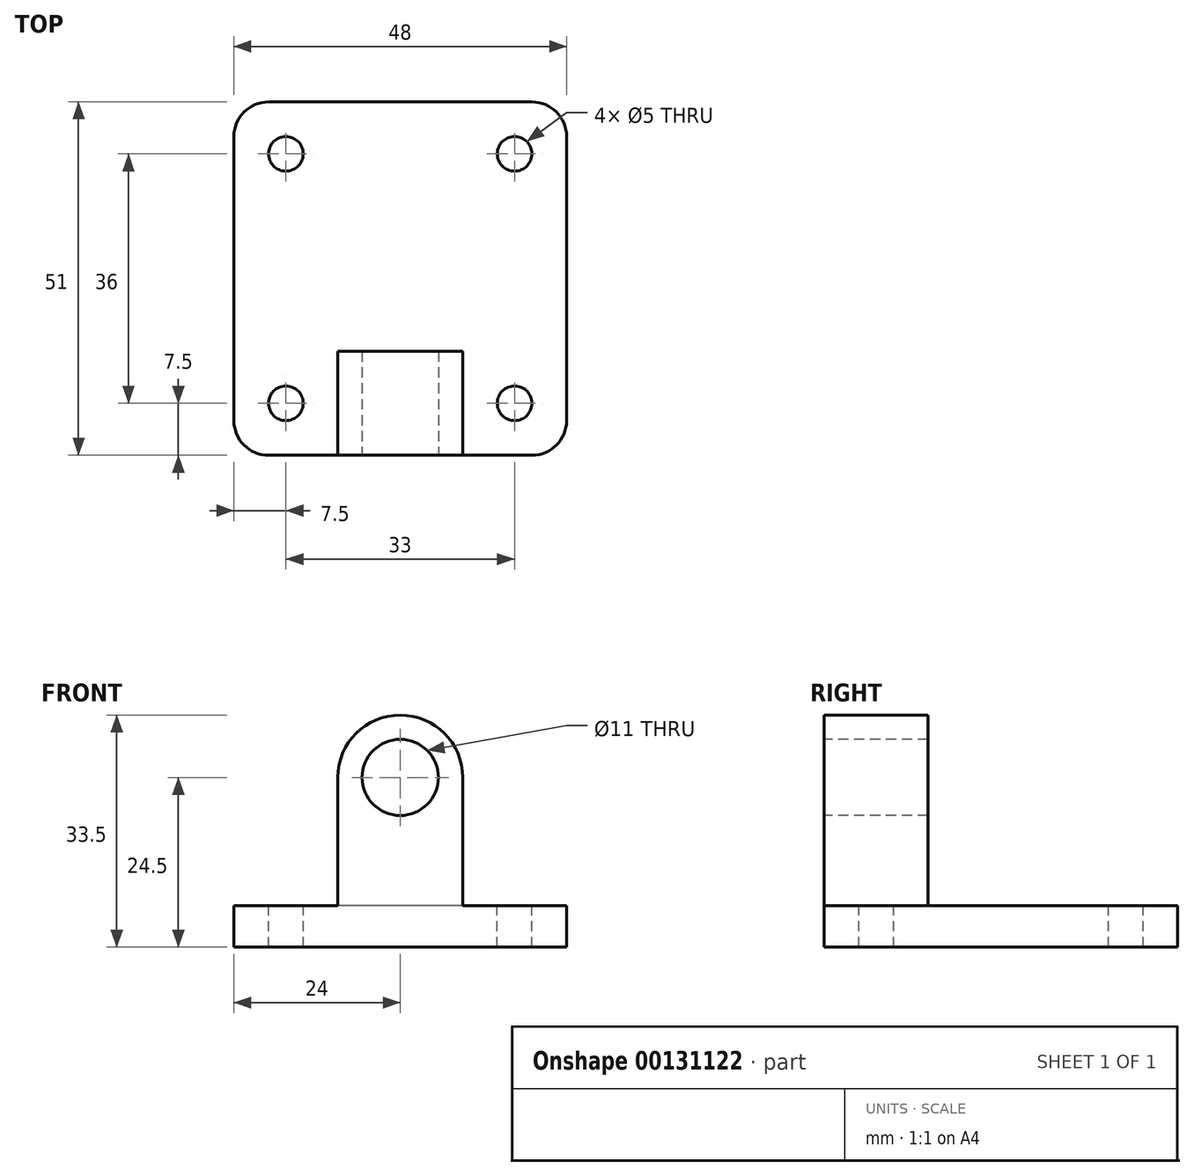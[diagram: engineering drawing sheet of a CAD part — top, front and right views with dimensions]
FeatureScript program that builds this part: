
annotation { "Feature Type Name" : "Feature", "Feature Type Description" : "" }
export const myFeature = defineFeature(function(context is Context, id is Id, definition is map)
    precondition{}
    {
        {
            var Q0;
            Q0=qCreatedBy(makeId("Top.planeOp"),FACE);
            var sketch = newSketch(context, id + "F0", { "sketchPlane" : qUnion([Q0])});
            skLineSegment(sketch, "E0.bottom", {"start": v(24, -7.75) * mm, "end": v(-24, -7.75) * mm});
            skLineSegment(sketch, "E0.top", {"start": v(24, 43.25) * mm, "end": v(-24, 43.25) * mm});
            skLineSegment(sketch, "E0.left", {"start": v(24, -7.75) * mm, "end": v(24, 43.25) * mm});
            skLineSegment(sketch, "E0.right", {"start": v(-24, -7.75) * mm, "end": v(-24, 43.25) * mm});
            skPoint(sketch, "E0.middle", {"position": v(-7.63, -98.95) * mm});
            skPoint(sketch, "E1", {"position": v(16.5, 35.75) * mm});
            skPoint(sketch, "E2", {"position": v(16.5, -0.25) * mm});
            skPoint(sketch, "E3", {"position": v(-16.5, 35.75) * mm});
            skPoint(sketch, "E4", {"position": v(-16.5, -0.25) * mm});
            skPoint(sketch, "E5.start.orphan", {"position": v(-7.63, -80.44) * mm});
            skPoint(sketch, "E6", {"position": v(10.17, -57.1) * mm});
            skPoint(sketch, "E7", {"position": v(-19.83, -57.1) * mm});
            skSolve(sketch);
        }
        {
            var Q0;
            Q0=makeQuery(id+"F0.imprint","IMPRINT",FACE,{"disambiguationData":[TD([[makeQuery(id+"F0.imprint","IMPRINT",EDGE,{"derivedFrom":sQuery(id+"F0.wireOp",EDGE,"E0.bottom")}),-1.0]])]});
            extrude(context, id + "F1", {"entities" : qUnion([Q0]), "oppositeDirection" : true, "depth" : 6 * mm});
        }
        {
            var Q0;
            Q0=makeQuery(id+"F1.opExtrude","SWEPT_EDGE",EDGE,{"disambiguationData":[OSD([sQuery(id+"F0.wireOp",EDGE,"E0.bottom"),sQuery(id+"F0.wireOp",EDGE,"E0.left")])]});
            var Q1;
            Q1=makeQuery(id+"F1.opExtrude","SWEPT_EDGE",EDGE,{"disambiguationData":[OSD([sQuery(id+"F0.wireOp",EDGE,"E0.top"),sQuery(id+"F0.wireOp",EDGE,"E0.left")])]});
            var Q2;
            Q2=makeQuery(id+"F1.opExtrude","SWEPT_EDGE",EDGE,{"disambiguationData":[OSD([sQuery(id+"F0.wireOp",EDGE,"E0.top"),sQuery(id+"F0.wireOp",EDGE,"E0.right")])]});
            var Q3;
            Q3=makeQuery(id+"F1.opExtrude","SWEPT_EDGE",EDGE,{"disambiguationData":[OSD([sQuery(id+"F0.wireOp",EDGE,"E0.bottom"),sQuery(id+"F0.wireOp",EDGE,"E0.right")])]});
            fillet(context, id + "F2", {"entities" : qUnion([Q0, Q1, Q2, Q3]), "radius" : 5 * mm, "tangentPropagation" : true, "allowEdgeOverflow" : false});
        }
        {
            var Q0;
            Q0=sQuery(id+"F0.wireOp",VERTEX,"E2");
            var Q1;
            Q1=sQuery(id+"F0.wireOp",VERTEX,"E4");
            var Q2;
            Q2=sQuery(id+"F0.wireOp",VERTEX,"E1");
            var Q3;
            Q3=sQuery(id+"F0.wireOp",VERTEX,"E3");
            var Q4;
            Q4=makeQuery(id+"F1.opExtrude","SWEPT_BODY",BODY,{"disambiguationData":[OSD([sQuery(id+"F0.wireOp",EDGE,"E0.bottom"),sQuery(id+"F0.wireOp",EDGE,"E0.top"),sQuery(id+"F0.wireOp",EDGE,"E0.left"),sQuery(id+"F0.wireOp",EDGE,"E0.right")])]});
            hole(context, id + "F3", {"style" : HoleStyle.SIMPLE, "endStyle" : HoleEndStyle.THROUGH, "holeDiameter" : 5 * mm, "locations" : qUnion([Q0, Q1, Q2, Q3]), "scope" : qUnion([Q4]), "isTappedThrough" : true});
        }
        {
            var Q0;
            Q0=makeQuery(id+"F1.opExtrude","SWEPT_FACE",FACE,{"disambiguationData":[OSD([sQuery(id+"F0.wireOp",EDGE,"E0.bottom")])]});
            var sketch = newSketch(context, id + "F4", { "sketchPlane" : qUnion([Q0])});
            skCircle(sketch, "E8", {"center": v(0, 18.5) * mm, "radius": 5.5 * mm});
            skArc(sketch, "E9", {"start": v(9, 18.5) * mm, "mid": v(0, 27.5) * mm, "end": v(-9, 18.5) * mm});
            skLineSegment(sketch, "E10", {"start": v(-9, 0) * mm, "end": v(-9, 18.5) * mm});
            skLineSegment(sketch, "E11", {"start": v(9, 0) * mm, "end": v(9, 18.5) * mm});
            skLineSegment(sketch, "E12", {"start": v(-9, 0) * mm, "end": v(9, 0) * mm});
            skSolve(sketch);
        }
        {
            var Q0;
            Q0=makeQuery(id+"F4.imprint","IMPRINT",FACE,{"disambiguationData":[TD([[makeQuery(id+"F4.imprint","IMPRINT",EDGE,{"derivedFrom":sQuery(id+"F4.wireOp",EDGE,"E8")}),-1.0]])]});
            extrude(context, id + "F5", {"entities" : qUnion([Q0]), "operationType" : NewBodyOperationType.ADD, "oppositeDirection" : true, "depth" : 15 * mm});
        }
    });
